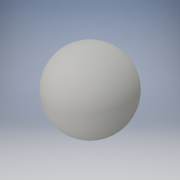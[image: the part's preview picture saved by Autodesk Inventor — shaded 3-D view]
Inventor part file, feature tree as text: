
AUTODESK INVENTOR PART (.ipt)
format: ipt  version: 2016 (Build 200138000, 138)  size: 113,664 bytes
history: native  units: in
note: dims shown in document units (in); Inventor stores cm internally (conversion verified against a paired STEP export)
features: revolve x1, sketch x1
ambient origin geometry x8: Origin, YZ Plane, XZ Plane, XY Plane, X Axis, Y Axis, Z Axis, Center Point
bodies: Solid1 (feature_tree)
feature tree (2):
  revolve  "Revolution1"  Angle=90.0deg
  sketch  "Sketch1"  dims[d0=0.715in d1=90.0deg]
